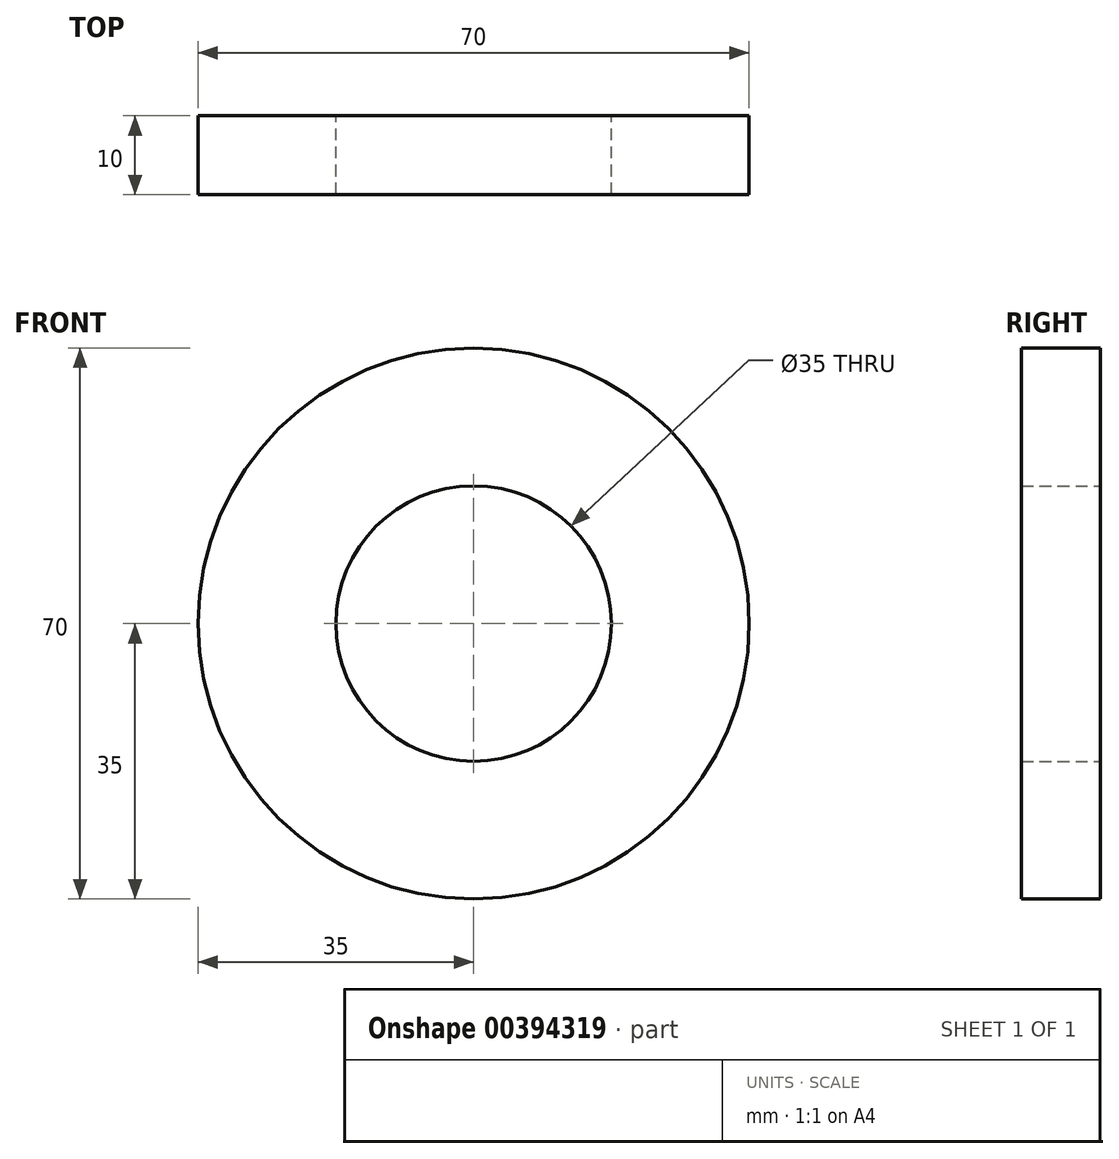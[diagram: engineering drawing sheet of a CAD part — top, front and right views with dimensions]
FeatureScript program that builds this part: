
annotation { "Feature Type Name" : "Feature", "Feature Type Description" : "" }
export const myFeature = defineFeature(function(context is Context, id is Id, definition is map)
    precondition{}
    {
        {
            var Q0;
            Q0=qCreatedBy(makeId("Front.planeOp"),FACE);
            var sketch = newSketch(context, id + "F0", { "sketchPlane" : qUnion([Q0])});
            skCircle(sketch, "E0", {"center": v(0, 0) * mm, "radius": 17.5 * mm});
            skCircle(sketch, "E1", {"center": v(0, 0) * mm, "radius": 35 * mm});
            skSolve(sketch);
        }
        {
            var Q0;
            Q0=sQuery(id+"F0.wireOp",EDGE,"E0");
            extrude(context, id + "F1", {"bodyType" : ToolBodyType.SURFACE, "surfaceEntities" : qUnion([Q0]), "depth" : 50 * mm});
        }
        {
            var Q0;
            Q0 = qSketchRegion(id + "F0", true);
            extrude(context, id + "F2", {"entities" : qUnion([Q0]), "depth" : 10 * mm});
        }
        {
            var Q0;
            Q0=makeQuery(id+"F1.opExtrude","CAP_EDGE",EDGE,{"disambiguationData":[OSD([sQuery(id+"F0.wireOp",EDGE,"E0")])],"isStart":false});
            var Q1;
            Q1=makeQuery(id+"F2.opExtrude","CAP_EDGE",EDGE,{"disambiguationData":[OSD([sQuery(id+"F0.wireOp",EDGE,"E1")])],"isStart":false});
            loft(context, id + "F3", {"bodyType" : ToolBodyType.SURFACE, "wireProfilesArray" : [{ "wireProfileEntities" : qUnion([Q0]) }, { "wireProfileEntities" : qUnion([Q1]) }]});
        }
    });
